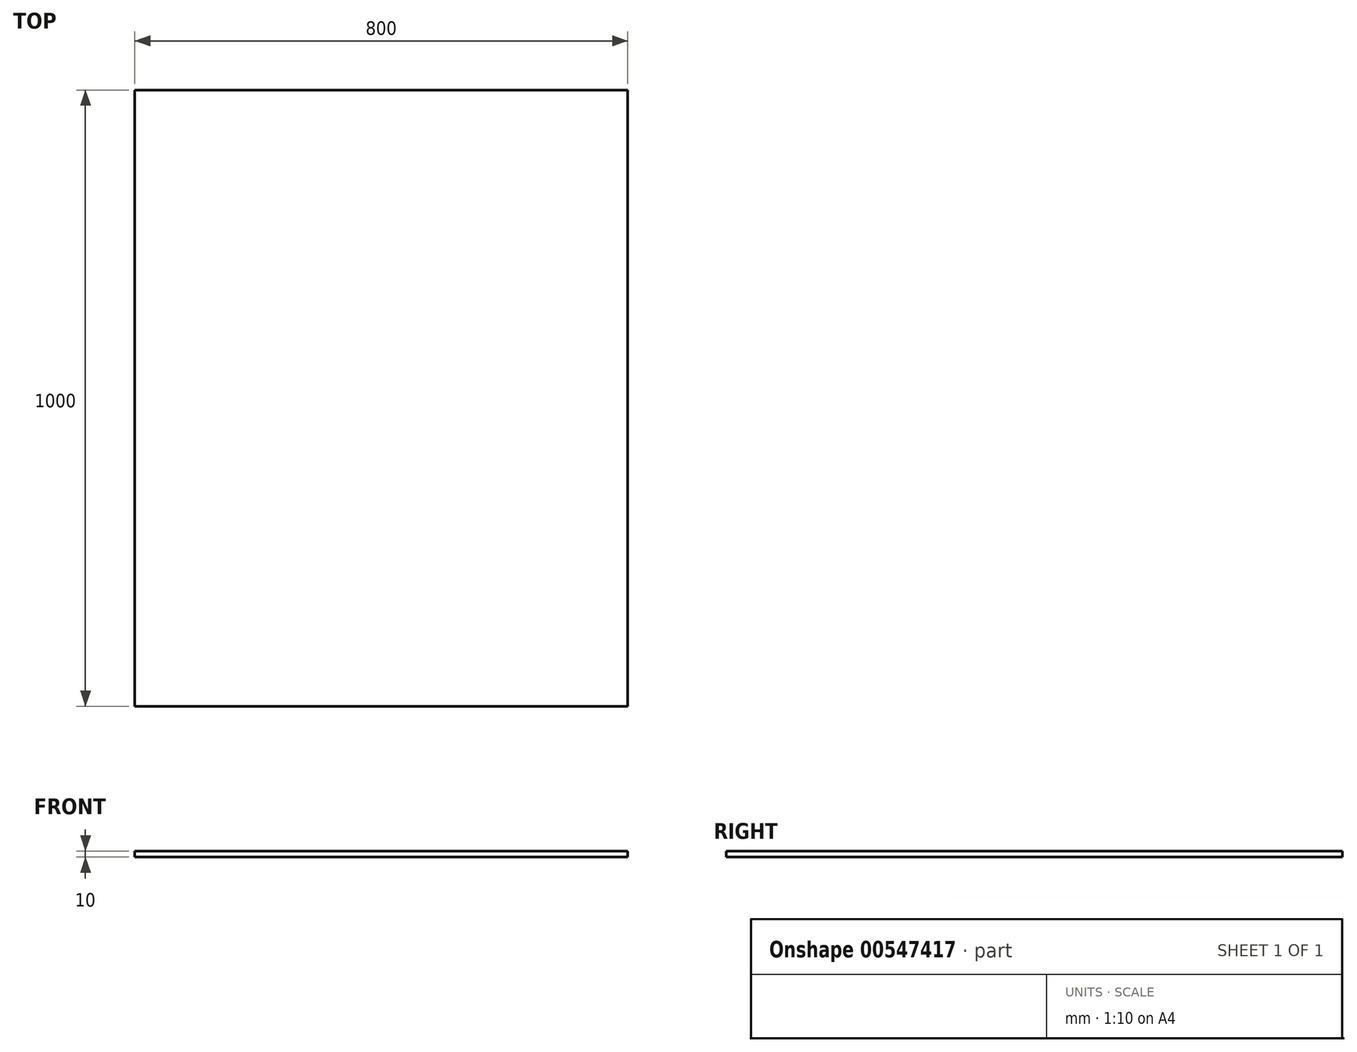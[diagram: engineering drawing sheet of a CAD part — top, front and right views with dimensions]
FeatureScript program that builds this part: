
annotation { "Feature Type Name" : "Feature", "Feature Type Description" : "" }
export const myFeature = defineFeature(function(context is Context, id is Id, definition is map)
    precondition{}
    {
        {
            var Q0;
            Q0=qCreatedBy(makeId("Top.planeOp"),FACE);
            var sketch = newSketch(context, id + "F0", { "sketchPlane" : qUnion([Q0])});
            skLineSegment(sketch, "E0.bottom", {"start": v(400, 500) * mm, "end": v(-400, 500) * mm});
            skLineSegment(sketch, "E0.top", {"start": v(400, -500) * mm, "end": v(-400, -500) * mm});
            skLineSegment(sketch, "E0.left", {"start": v(400, 500) * mm, "end": v(400, -500) * mm});
            skLineSegment(sketch, "E0.right", {"start": v(-400, 500) * mm, "end": v(-400, -500) * mm});
            skPoint(sketch, "E0.middle", {"position": v(0, 0) * mm});
            skSolve(sketch);
        }
        {
            var Q0;
            Q0 = qSketchRegion(id + "F0", true);
            extrude(context, id + "F1", {"entities" : qUnion([Q0]), "endBound" : BoundingType.SYMMETRIC, "depth" : 10 * mm, "offsetDistance" : 25 * mm});
        }
    });
